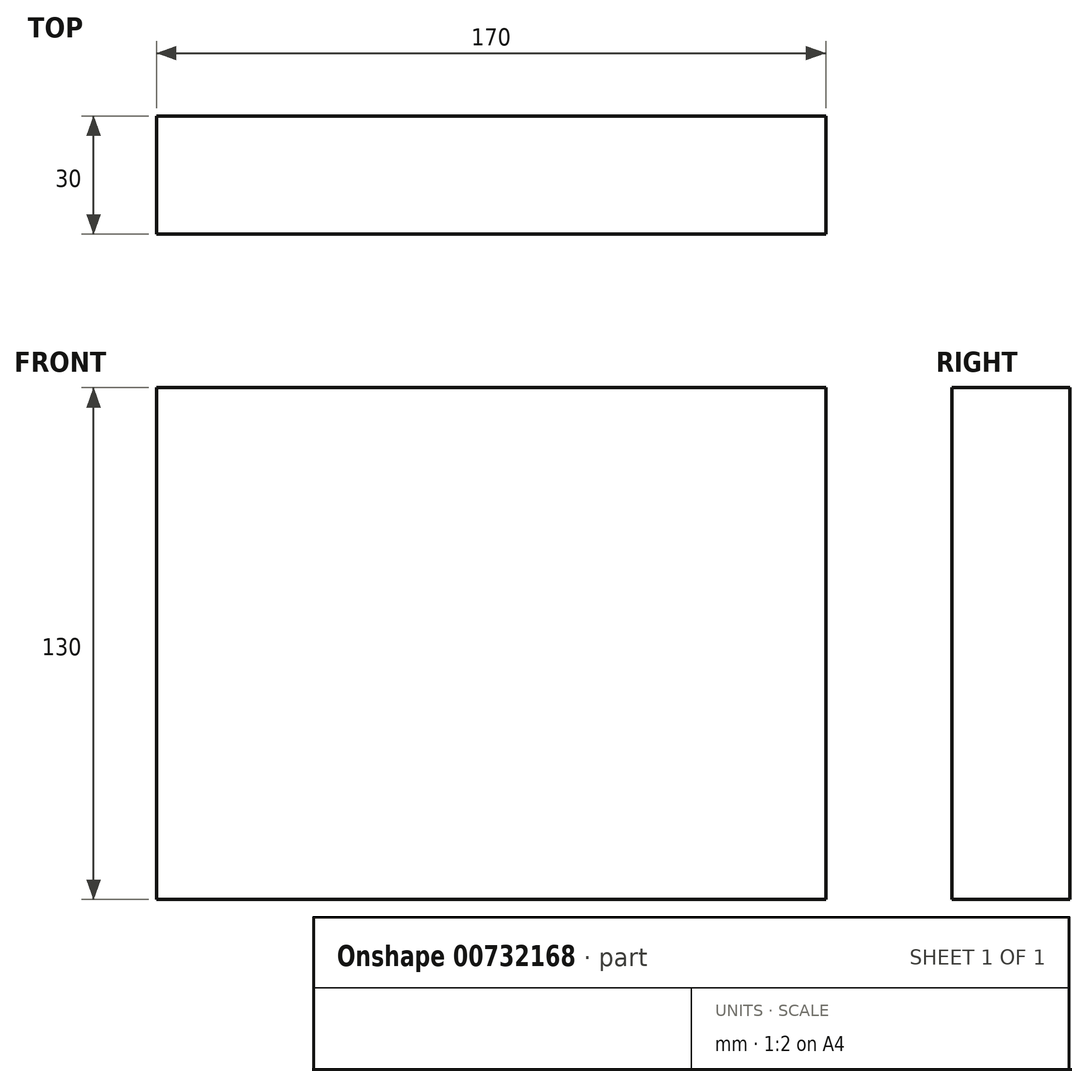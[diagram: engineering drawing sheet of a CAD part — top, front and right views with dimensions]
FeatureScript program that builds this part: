
annotation { "Feature Type Name" : "Feature", "Feature Type Description" : "" }
export const myFeature = defineFeature(function(context is Context, id is Id, definition is map)
    precondition{}
    {
        {
            var Q0;
            Q0=qCreatedBy(makeId("Front.planeOp"),FACE);
            var sketch = newSketch(context, id + "F0", { "sketchPlane" : qUnion([Q0])});
            skLineSegment(sketch, "E0.bottom", {"start": v(0, 0) * mm, "end": v(170, 0) * mm});
            skLineSegment(sketch, "E0.top", {"start": v(0, 130) * mm, "end": v(170, 130) * mm});
            skLineSegment(sketch, "E0.left", {"start": v(0, 0) * mm, "end": v(0, 130) * mm});
            skLineSegment(sketch, "E0.right", {"start": v(170, 0) * mm, "end": v(170, 130) * mm});
            skSolve(sketch);
        }
        {
            var Q0;
            Q0=makeQuery(id+"F0.imprint","IMPRINT",FACE,{"disambiguationData":[TD([[makeQuery(id+"F0.imprint","IMPRINT",EDGE,{"derivedFrom":sQuery(id+"F0.wireOp",EDGE,"E0.bottom")}),1.0]])]});
            extrude(context, id + "F1", {"entities" : qUnion([Q0]), "depth" : 30 * mm, "offsetDistance" : 25 * mm});
        }
    });
